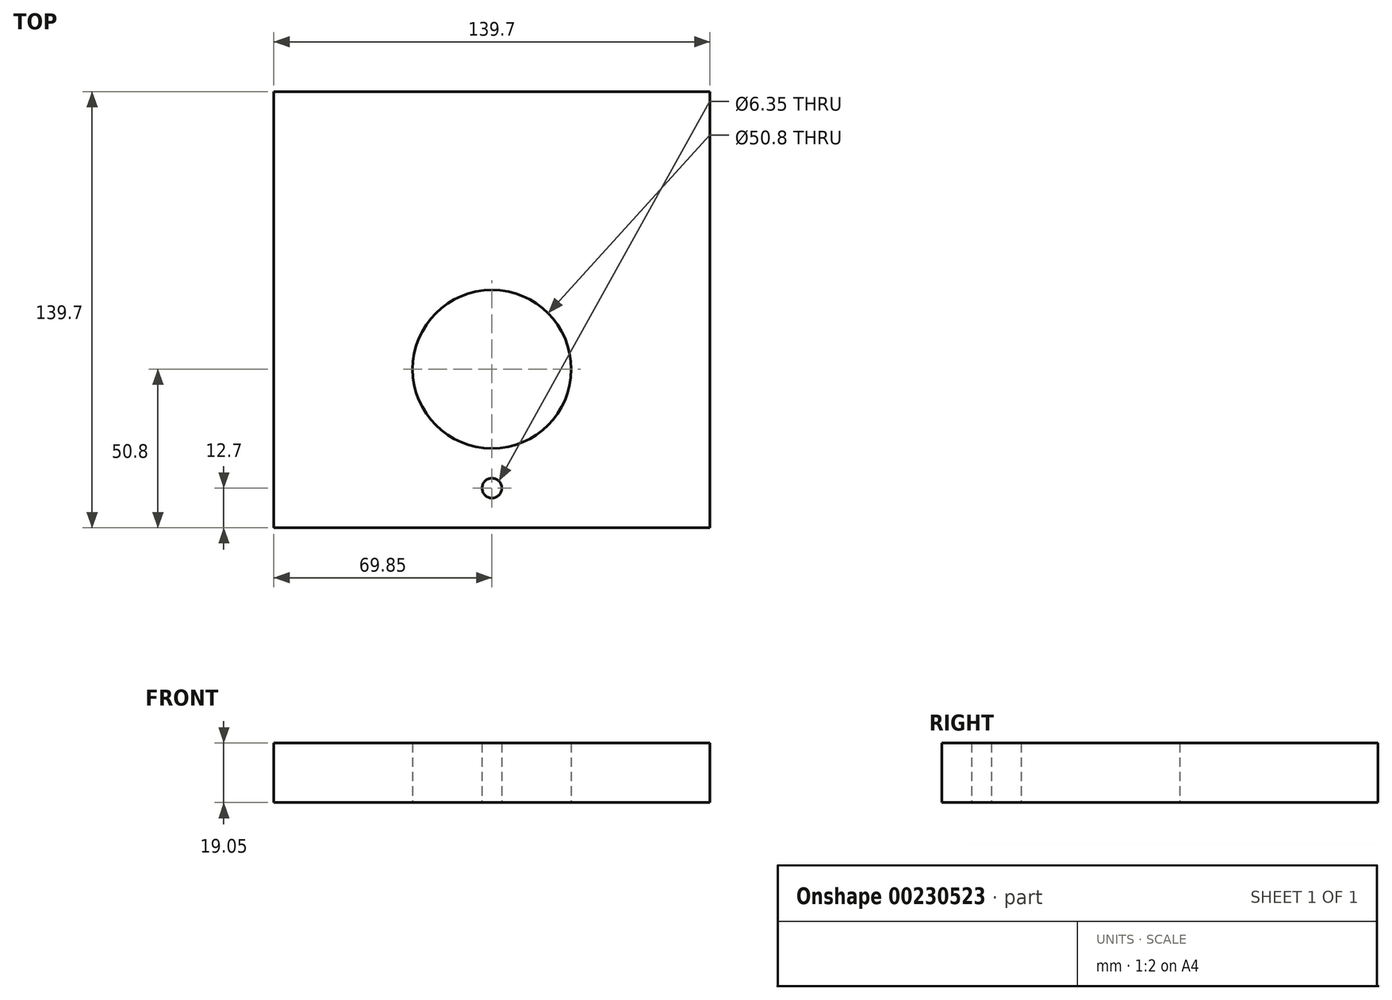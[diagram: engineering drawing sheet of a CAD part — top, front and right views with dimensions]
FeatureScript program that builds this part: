
annotation { "Feature Type Name" : "Feature", "Feature Type Description" : "" }
export const myFeature = defineFeature(function(context is Context, id is Id, definition is map)
    precondition{}
    {
        {
            var Q0;
            Q0=qCreatedBy(makeId("Top.planeOp"),FACE);
            var sketch = newSketch(context, id + "F0", { "sketchPlane" : qUnion([Q0])});
            skLineSegment(sketch, "E0.bottom", {"start": v(-69.85, 69.85) * mm, "end": v(69.85, 69.85) * mm});
            skLineSegment(sketch, "E0.top", {"start": v(-69.85, -69.85) * mm, "end": v(69.85, -69.85) * mm});
            skLineSegment(sketch, "E0.left", {"start": v(-69.85, 69.85) * mm, "end": v(-69.85, -69.85) * mm});
            skLineSegment(sketch, "E0.right", {"start": v(69.85, 69.85) * mm, "end": v(69.85, -69.85) * mm});
            skPoint(sketch, "E0.middle", {"position": v(0, 0) * mm});
            skLineSegment(sketch, "E1", {"start": v(0, -69.85) * mm, "end": v(0, -57.15) * mm});
            skPoint(sketch, "E1.endSnap0", {"position": v(0, -69.85) * mm});
            skCircle(sketch, "E2", {"center": v(0, -57.15) * mm, "radius": 3.18 * mm});
            skLineSegment(sketch, "E3", {"start": v(0, -57.15) * mm, "end": v(0, -19.05) * mm});
            skCircle(sketch, "E4", {"center": v(0, -19.05) * mm, "radius": 25.4 * mm});
            skSolve(sketch);
        }
        {
            var Q0;
            Q0=makeQuery(id+"F0.imprint","IMPRINT",FACE,{"disambiguationData":[TD([[makeQuery(id+"F0.imprint","IMPRINT",EDGE,{"derivedFrom":sQuery(id+"F0.wireOp",EDGE,"E0.bottom")}),-1.0]])]});
            extrude(context, id + "F1", {"entities" : qUnion([Q0]), "depth" : 19.05 * mm});
        }
    });
